# Revit family: Furniture_Shelving&Storage_Sjobergs_Cabinet_1
name_source: partatom
category: Furniture
revit_build: Autodesk Revit 2017 (Build: 20160225_1515(x64)
units: mm (PartAtom-declared; Revit-internal decimal feet)

## family parameters
Always vertical = Yes
Cut with Voids When Loaded = No
OmniClass Number = 23.40.20.27.21
OmniClass Title = Mobile Storage Units
Room Calculation Point = No
Shared = No
Work Plane-Based = No

## types (1)
- 33001 Sjobergs Complete Cabinet 1
    AssetType = Movable
    BIMObjectName = Furniture_Shelving&Storage_Sjobergs_Cabinet_1
    Brand = Sjobergs
    Category = Cabinets
    Collection = Cabinet
    Color = Wooden
    ConvergoRefNr = 0184-2005-0011-SE
    Cost = 0 $
    Description = A sturdy, attractive and smart storage closet. 18 mm birch plywood frame and interior both stability and durability. Doors designed so that you can push them easily with the side of the closet. There are no more swinging doors inside about. Sjoberg cabinets can be decorated in many different ways to meet the need for storage of tools, textiles, office supplies, computers, etc.
    DrawerTertiaryMaterial = Clearance
    Features = This wardrobe is available in 8 finished versions.  Assembling the cabinets is very simple, installation instructions are included in the packages. We also supply pre-assembled cabinets surcharge. The cabinets come unassembled in the flat package, knock down.
    Finish = Beech plywood 18 mm, doors in birch laminate
    IfcExportAs = IfcFurnitureType
    IfcExportType = DRAWER
    MainColor = Wooden
    ManufacterURL = https://www.sjobergs.se
    Manufacturer = Sjobergs
    ManufacturerName = Sjobergs
    Material = Wood
    Model = 33001 Sjobergs Complete Cabinet 1
    ModelNumber = 33001
    NBSDescription = Cabinets
    NBSReference = 45-35-47/415
    Name = Sjobergs_Cabinet_1
    NominalDepth = 593 mm
    NominalHeight = 2100 mm
    NominalWidth = 1000 mm  [stored 3.28084 ft]
    ProductDatasheet = https://www.sjobergs.se
    ProductInformation = A sturdy, attractive and smart storage closet. 18 mm birch plywood frame and interior both stability and durability. Doors designed so that you can push them easily with the side of the closet. There are no more swinging doors inside about. Sjoberg cabinets can be decorated in many different ways to meet the need for storage of tools, textiles, office supplies, computers, etc.
    Shape = Sculptured
    Size = 1000x490x2100 mm
    URL = https://www.sjobergs.se
    Uniclass2 = Pr_40_30_78_24
    Uniclass2015Description = Storage units
    Uniclass2015Reference = Pr_40_30_78_25
    Version = 1
    VersionDate = 30/06/2020

note: [stored X ft] marks values corroborated as IEEE doubles in the binary element streams (Revit-internal decimal feet)

## geometry (parser evidence)
native form markers: Sweep x4
no freeform markers — native parametric forms only
